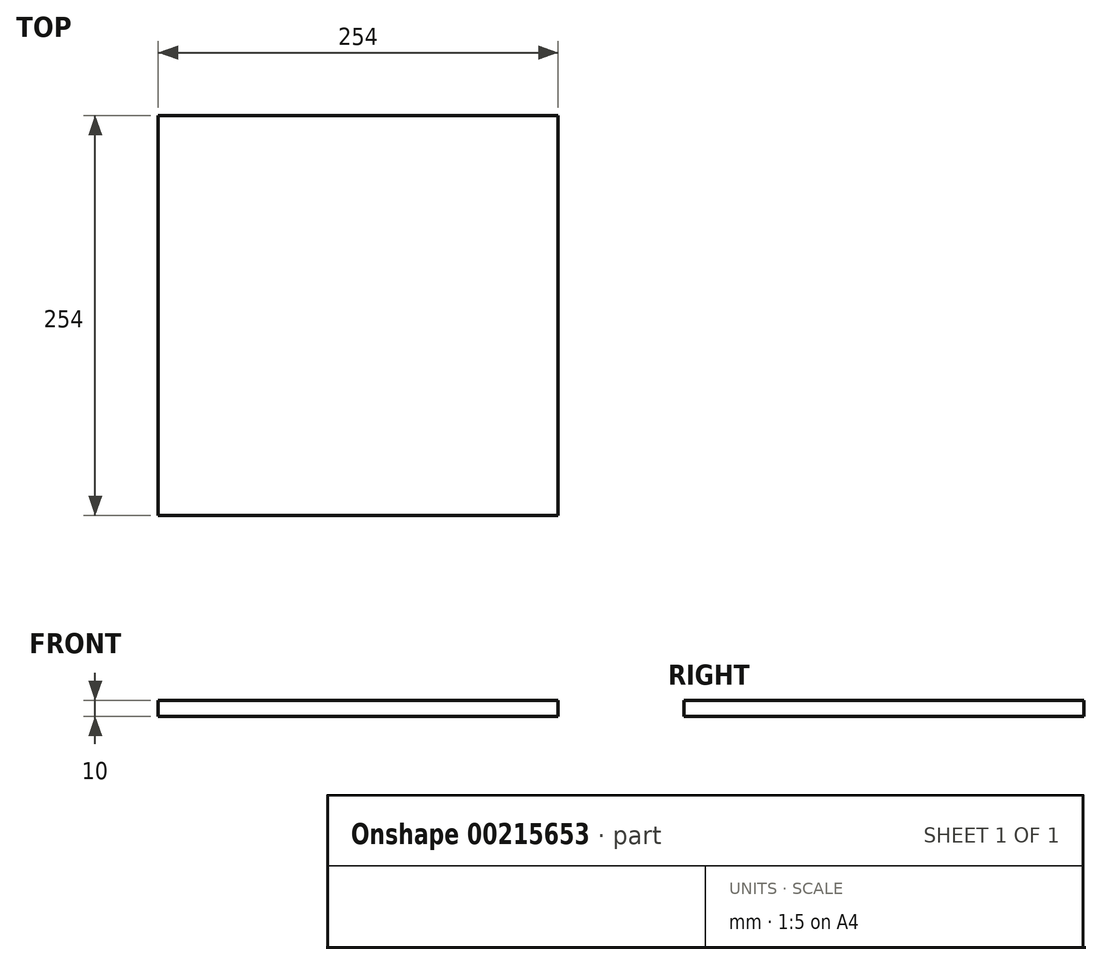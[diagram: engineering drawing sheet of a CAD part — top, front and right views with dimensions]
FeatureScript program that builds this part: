
annotation { "Feature Type Name" : "Feature", "Feature Type Description" : "" }
export const myFeature = defineFeature(function(context is Context, id is Id, definition is map)
    precondition{}
    {
        {
            assignVariable(context, id + "F0", {"name" : "Cube", "anyValue" : 10});
        }
        {
            var Q0;
            Q0=qCreatedBy(makeId("Top.planeOp"),FACE);
            var sketch = newSketch(context, id + "F1", { "sketchPlane" : qUnion([Q0])});
            skLineSegment(sketch, "E0.bottom", {"start": v(0, 0) * mm, "end": v(254, 0) * mm});
            skLineSegment(sketch, "E0.top", {"start": v(0, 254) * mm, "end": v(254, 254) * mm});
            skLineSegment(sketch, "E0.left", {"start": v(0, 0) * mm, "end": v(0, 254) * mm});
            skLineSegment(sketch, "E0.right", {"start": v(254, 0) * mm, "end": v(254, 254) * mm});
            skSolve(sketch);
        }
        {
            var Q0;
            Q0=makeQuery(id+"F1.imprint","IMPRINT",FACE,{"disambiguationData":[TD([[makeQuery(id+"F1.imprint","IMPRINT",EDGE,{"derivedFrom":sQuery(id+"F1.wireOp",EDGE,"E0.bottom")}),1.0]])]});
            extrude(context, id + "F2", {"entities" : qUnion([Q0]), "depth" : (getVariable(context, 'Cube')) * mm});
        }
    });
